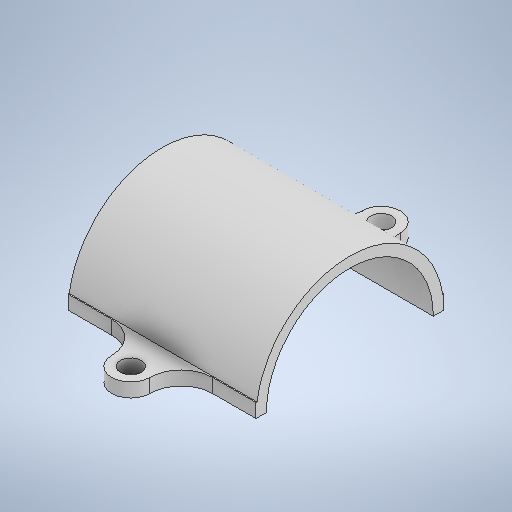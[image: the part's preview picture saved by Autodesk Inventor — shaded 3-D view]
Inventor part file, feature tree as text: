
AUTODESK INVENTOR PART (.ipt)
format: ipt  version: 2025.2 (Build 292293000, 293)  size: 291,840 bytes
history: native  units: mm
features: sketch x4, extrude x3, other x1, hole x1
ambient origin geometry x8: Origin, YZ Plane, XZ Plane, XY Plane, X Axis, Y Axis, Z Axis, Center Point
bodies: Body1 (feature_tree)
feature tree (9):
  other  "ソリッド1"
  extrude  "押し出し1"  Depth=27.0mm
  extrude  "押し出し2"  Depth=5.5mm
  hole  "穴1"  [1 undecoded]
  extrude  "押し出し3"  Depth=4.5mm
  sketch  "スケッチ1"
  sketch  "スケッチ2"
  sketch  "スケッチ3"
  sketch  "スケッチ4"
note: 1 required parameter value undecoded (feature->parameter linkage not recoverable at this tier; creation-order binding heuristic only, values carry confidence <= 0.55)
